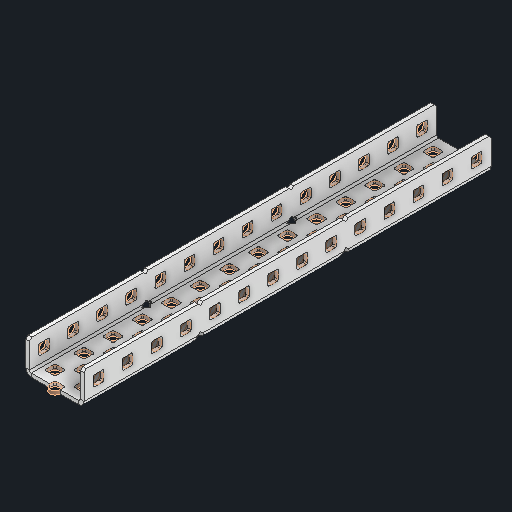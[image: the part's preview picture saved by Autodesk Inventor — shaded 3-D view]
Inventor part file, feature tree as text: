
AUTODESK INVENTOR PART (.ipt)
format: ipt  version: 2024 (Build 280153000, 153)  size: 1,235,456 bytes
history: native  units: in
note: dims shown in document units (in); Inventor stores cm internally (conversion verified against a paired STEP export)
features: other x146, sketch x5, sheet_metal_op x1
ambient origin geometry x8: Origin, YZ Plane, XZ Plane, XY Plane, X Axis, Y Axis, Z Axis, Center Point
bodies: Solid1 (feature_tree)
feature tree (152):
  other  "Alu C 1x2x1x14.ipt"
  other  "Solid1::Alu C 1x2x1x14.ipt"
  other  "TaggingFeature1"
  sketch  "Sketch1"  dims[d0=0.3937in]
  sketch  "Sketch2"  dims[d1=0.0625in]
  sketch  "Sketch3"
  other  "Flange Pattern Sketch"
  sketch  "Sketch9"
  sheet_metal_op  "Body Pattern Sketch"
  other  "Arc Length"
  sketch  "Sketch14"
  other  "Flange Pattern Plane"
  other  "Srf1"
  other  "Srf2"
  other  "Srf3"
  other  "Srf4"
  other  "Srf5"
  other  "Srf6"
  other  "Srf7"
  other  "Srf8"
  other  "Srf9"
  other  "Srf10"
  other  "Srf11"
  other  "Srf12"
  other  "Srf13"
  other  "Srf14"
  other  "Srf15"
  other  "Srf16"
  other  "Srf17"
  other  "Srf18"
  other  "Srf19"
  other  "Srf20"
  other  "Srf21"
  other  "Srf22"
  other  "Srf23"
  other  "Srf24"
  other  "Srf25"
  other  "Srf26"
  other  "Srf27"
  other  "Srf28"
  other  "Srf29"
  other  "Srf30"
  other  "Srf31"
  other  "Srf32"
  other  "Srf33"
  other  "Srf34"
  other  "Srf35"
  other  "Srf36"
  other  "Srf37"
  other  "Srf38"
  other  "Srf39"
  other  "Srf40"
  other  "Srf41"
  other  "Srf42"
  other  "Srf43"
  other  "Srf44"
  other  "Srf45"
  other  "Srf46"
  other  "Srf47"
  other  "Srf48"
  other  "Srf49"
  other  "Srf50"
  other  "Srf51"
  other  "Srf52"
  other  "Srf53"
  other  "Srf54"
  other  "Srf55"
  other  "Srf56"
  other  "Srf57"
  other  "Srf58"
  other  "Srf59"
  other  "Srf60"
  other  "Srf61"
  other  "Srf62"
  other  "Srf63"
  other  "Srf64"
  other  "Srf65"
  other  "Srf66"
  other  "Srf67"
  other  "Srf68"
  other  "Srf69"
  other  "Srf70"
  other  "Srf1::Derived"
  other  "Srf2::Derived"
  other  "Srf823::Derived"
  other  "Srf824::Derived"
  other  "Srf825::Derived"
  other  "Srf826::Derived"
  other  "Srf827::Derived"
  other  "Srf828::Derived"
  other  "Srf829::Derived"
  other  "Srf922::Derived"
  other  "Srf923::Derived"
  other  "Srf924::Derived"
  other  "Srf925::Derived"
  other  "Srf926::Derived"
  other  "Srf1143::Derived"
  other  "Srf1144::Derived"
  other  "Srf1145::Derived"
  other  "Srf1146::Derived"
  other  "Srf1147::Derived"
  other  "Srf1148::Derived"
  other  "Srf1149::Derived"
  other  "Srf1150::Derived"
  other  "Srf1151::Derived"
  other  "Srf1152::Derived"
  other  "Srf1153::Derived"
  other  "Srf1154::Derived"
  other  "Srf1155::Derived"
  other  "Srf1156::Derived"
  other  "Srf91::Derived"
  other  "Srf92::Derived"
  other  "Srf856::Derived"
  other  "Srf857::Derived"
  other  "Srf858::Derived"
  other  "Srf859::Derived"
  other  "Srf860::Derived"
  other  "Srf861::Derived"
  other  "Srf862::Derived"
  other  "Srf959::Derived"
  other  "Srf960::Derived"
  other  "Srf961::Derived"
  other  "Srf962::Derived"
  other  "Srf963::Derived"
  other  "Srf1199::Derived"
  other  "Srf1200::Derived"
  other  "Srf1201::Derived"
  other  "Srf1202::Derived"
  other  "Srf1203::Derived"
  other  "Srf1204::Derived"
  other  "Srf1205::Derived"
  other  "Srf1206::Derived"
  other  "Srf1207::Derived"
  other  "Srf1208::Derived"
  other  "Srf1209::Derived"
  other  "Srf1210::Derived"
  other  "Srf1211::Derived"
  other  "Srf1212::Derived"
  other  "Srf786::Derived"
  other  "Srf889::Derived"
  other  "Srf890::Derived"
  other  "Srf891::Derived"
  other  "Srf892::Derived"
  other  "Srf893::Derived"
  other  "Srf894::Derived"
  other  "Srf895::Derived"
  other  "Srf896::Derived"
  other  "Srf996::Derived"
  other  "Srf997::Derived"
  other  "Srf998::Derived"
  other  "Srf999::Derived"
  other  "Srf1000::Derived"
